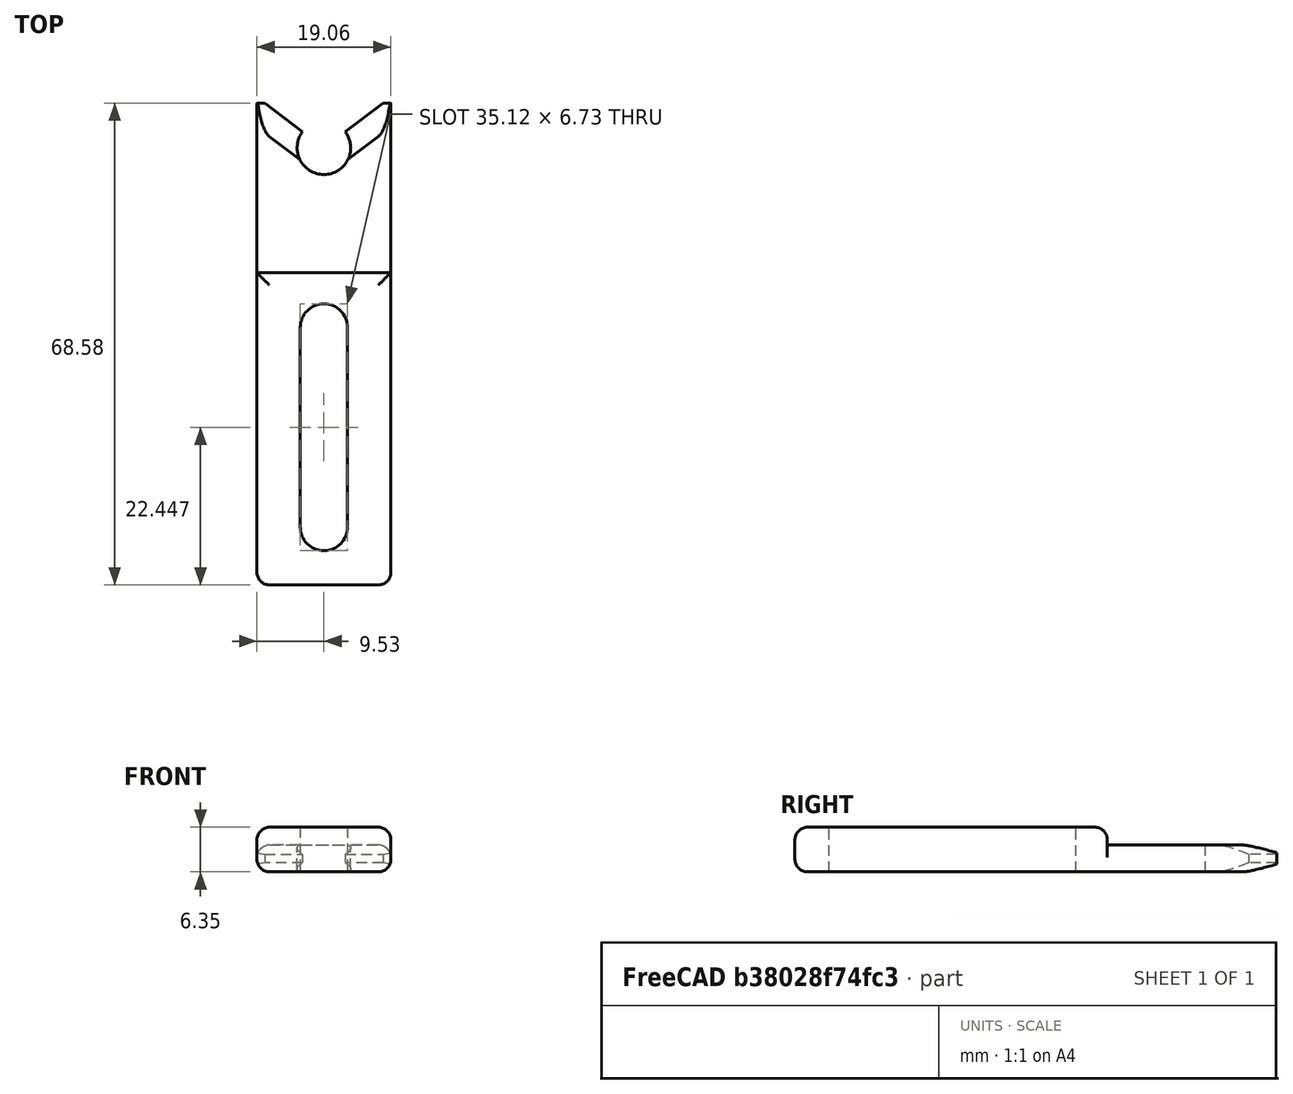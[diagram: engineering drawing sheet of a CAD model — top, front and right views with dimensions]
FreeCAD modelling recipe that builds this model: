
FCSTD DOCUMENT  (FreeCAD 0.18R16110 (Git))
Label: Headfixing clamp remodeled
License: All rights reserved
LicenseURL: http://en.wikipedia.org/wiki/All_rights_reserved
objects: Sketcher::SketchObject×6, PartDesign::SubtractivePipe×2, PartDesign::Pad×1, PartDesign::Pocket×1, Mesh::Feature×1, Part::Feature×1, PartDesign::Fillet×1, PartDesign::Body×1
note: 17 computed .brp shape members not serialized (recipe doc carries the construction recipe); baked Part::Feature solids carry a one-line shape summary decoded from their .brp

FEATURE [Sketcher::SketchObject] Sketch  label="Main body"
  MapMode = 5
  Placement = pos=(0,0,0) rot=(0.57735,0.57735,0.57735;2.0944rad)
  sketch-geometry (6):
    g0: LineSegment StartX=-62.23 StartY=6.35 StartZ=0 EndX=-17.78 EndY=6.35 EndZ=0
    g1: LineSegment StartX=-17.78 StartY=6.35 StartZ=0 EndX=-17.78 EndY=3.81 EndZ=0
    g2: LineSegment StartX=-17.78 StartY=3.81 StartZ=0 EndX=6.35 EndY=3.81 EndZ=0
    g3: LineSegment StartX=6.35 StartY=3.81 StartZ=0 EndX=6.35 EndY=0 EndZ=0
    g4: LineSegment StartX=6.35 StartY=0 StartZ=0 EndX=-62.23 EndY=0 EndZ=0
    g5: LineSegment StartX=-62.23 StartY=0 StartZ=0 EndX=-62.23 EndY=6.35 EndZ=0
  constraints (18):
    c: Coincident(g0,g1)
    c: Coincident(g1,g2)
    c: Coincident(g2,g3)
    c: Coincident(g3,g4)
    c: Coincident(g4,g5)
    c: Coincident(g0,g5)
    c: Vertical(g5)
    c: Vertical(g1)
    c: Vertical(g3)
    c: Horizontal(g0)
    c: Horizontal(g2)
    c: Horizontal(g4)
    c: DistanceY(g4) = 0
    c: Distance(g5) = 6.35
    c: DistanceX(g0) = -62.23
    c: Distance(g3) = 3.81
    c: DistanceX(g0) = -17.78
    c: DistanceX(g2) = 6.35
FEATURE [Sketcher::SketchObject] Sketch001  label="Cutouts"
  MapMode = 5
  Placement = pos=(-1e-15,0,6.35) rot=(0,0,-1;1.5708rad)
  expr: Constraints[6] = 0.265" / 2
  expr: Constraints[7] = 1.3825" - 2 * 0.1325"
  expr: Constraints[8] = 0.875" + 0.1325"
  expr: Constraints[11] = 0.331761"
  sketch-geometry (10):
    g0: ArcOfCircle CenterX=25.5905 CenterY=0 CenterZ=0 NormalX=0 NormalY=0 NormalZ=1 AngleXU=0 Radius=3.3655 StartAngle=1.5708 EndAngle=4.71239
    g1: ArcOfCircle CenterX=53.975 CenterY=0 CenterZ=0 NormalX=0 NormalY=0 NormalZ=1 AngleXU=0 Radius=3.3655 StartAngle=4.71239 EndAngle=7.85398
    g2: LineSegment StartX=25.5905 StartY=-3.3655 StartZ=0 EndX=53.975 EndY=-3.3655 EndZ=0
    g3: LineSegment StartX=25.5905 StartY=3.3655 StartZ=0 EndX=53.975 EndY=3.3655 EndZ=0
    g4: LineSegment [constr] StartX=-6.35 StartY=8.42673 StartZ=0 EndX=9e-16 EndY=0 EndZ=0
    g5: LineSegment [constr] StartX=0 StartY=0 StartZ=0 EndX=-6.35 EndY=-8.42673 EndZ=0
    g6: ArcOfCircle CenterX=0 CenterY=0 CenterZ=0 NormalX=0 NormalY=0 NormalZ=1 AngleXU=0 Radius=3.81 StartAngle=4.06662 EndAngle=8.49975
    g7: LineSegment StartX=-2.29292 StartY=-3.0428 StartZ=0 EndX=-6.35 EndY=-8.42673 EndZ=0
    g8: LineSegment StartX=-6.35 StartY=-8.42673 StartZ=0 EndX=-6.35 EndY=8.42673 EndZ=0
    g9: LineSegment StartX=-6.35 StartY=8.42673 StartZ=0 EndX=-2.29292 EndY=3.0428 EndZ=0
  constraints (25):
    c: Tangent(g0,g3) = 1.5708
    c: Tangent(g0,g2) = -1.5708
    c: Tangent(g2,g1) = -1.5708
    c: Tangent(g3,g1) = 1.5708
    c: Horizontal(g2)
    c: Equal(g0,g1)
    c: Radius(g0) = 3.3655
    c: DistanceX(g0,g1) = 28.3845
    c: DistanceX(g0) = 25.5905
    c: DistanceY(g0) = 0
    c: Symmetric(g4,g5,g-1)
    c: DistanceY(g4) = 8.42673
    c: DistanceX(g4) = -6.35
    c: Coincident(g4,g5)
    c: Coincident(g4,g6)
    c: Coincident(g4,g-1)
    c: Radius(g6) = 3.81
    c: Symmetric(g6,g6,g-1)
    c: Coincident(g7,g8)
    c: Coincident(g8,g9)
    c: Coincident(g6,g9)
    c: Coincident(g6,g7)
    c: Coincident(g5,g7)
    c: Coincident(g4,g8)
    c: Parallel(g9,g4)
FEATURE [PartDesign::Pad] Pad
  Length = 19.05
  Length2 = 99.9998
  Midplane = true
  Placement = pos=(0,0,0) rot=(0.57735,0.57735,0.57735;2.0944rad)
  Profile = -> Sketch
  Type = 0
FEATURE [PartDesign::Pocket] Pocket
  BaseFeature = -> Pad
  Length = 5.00126
  Length2 = 99.9998
  Placement = pos=(0,0,0) rot=(0.57735,0.57735,0.57735;2.0944rad)
  Profile = -> Sketch001
  Type = 1
FEATURE [Mesh::Feature] wide_post_clamp_with_slot_rescaled  label="wide post clamp with slot rescaled"
FEATURE [Part::Feature] wide_post_clamp_with_slot_rescaled001
  shape: bbox 19.05 x 68.58 x 6.35 mm, 1280 faces, 0 solids (baked)
FEATURE [Sketcher::SketchObject] Sketch002  label="Clamp V profile"
  MapMode = 5
  Placement = pos=(4e-16,6.35,-4e-16) rot=(0.57735,0.57735,0.57735;4.18879rad)
  Support = -> [Pocket]
  sketch-geometry (7):
    g0: LineSegment StartX=1.3335 StartY=-8.382 StartZ=0 EndX=2.4765 EndY=-8.382 EndZ=0
    g1: LineSegment StartX=2.4765 StartY=-8.382 StartZ=0 EndX=4.59972 EndY=-17.399 EndZ=0
    g2: LineSegment StartX=3.4925 StartY=-7.874 StartZ=0 EndX=0.3175 EndY=-7.874 EndZ=0
    g3: LineSegment StartX=-0.789722 StartY=-17.399 StartZ=0 EndX=1.3335 EndY=-8.382 EndZ=0
    g4: LineSegment [constr] StartX=1.905 StartY=0 StartZ=0 EndX=1.905 EndY=-6.35 EndZ=0
    g5: LineSegment StartX=-0.789722 StartY=-17.399 StartZ=0 EndX=0.3175 EndY=-7.874 EndZ=0
    g6: LineSegment StartX=4.59972 StartY=-17.399 StartZ=0 EndX=3.4925 EndY=-7.874 EndZ=0
  constraints (19):
    c: Coincident(g0,g1)
    c: DistanceY(g4) = -6.35
    c: DistanceX(g4) = 1.905
    c: Vertical(g4)
    c: DistanceY(g4) = 0
    c: Symmetric(g3,g1,g4)
    c: Coincident(g0,g3)
    c: Symmetric(g0,g0,g4)
    c: Angle(g3,g1) = 0.462512
    c: DistanceX(g0,g0) = 1.143
    c: DistanceY(g0,g2) = 0.508
    c: DistanceY(g0) = -8.382
    c: DistanceY(g3,g2) = 9.525
    c: Symmetric(g2,g2,g4)
    c: Coincident(g2,g6)
    c: Coincident(g1,g6)
    c: Coincident(g3,g5)
    c: Coincident(g5,g2)
    c: DistanceX(g2,g2) = 3.175
FEATURE [Sketcher::SketchObject] Sketch003  label="Clamp V path"
  MapMode = 5
  Placement = pos=(1e-16,1e-16,0) rot=(0.666877,0.332492,0.666877;3.78358rad)
  Support = -> [Pocket]
  sketch-geometry (1):
    g0: LineSegment StartX=0 StartY=-10.668 StartZ=0 EndX=0 EndY=3.175 EndZ=0
  constraints (4):
    c: DistanceX(g0) = 0
    c: DistanceY(g0) = -10.668
    c: Vertical(g0)
    c: DistanceY(g0) = 3.175
FEATURE [PartDesign::SubtractivePipe] SubtractivePipe
  AuxilleryCurvelinear = true
  AuxillerySpineTangent = false
  BaseFeature = -> Pocket
  Binormal = (0,0,0)
  Mode = 0
  Placement = pos=(0,0,0) rot=(0.57735,0.57735,0.57735;2.0944rad)
  Profile = -> Sketch002
  Spine = -> Sketch003 [Edge1]
  SpineTangent = false
  Transformation = 0
  Transition = 0
FEATURE [Sketcher::SketchObject] Sketch004  label="Clamp V profile001"
  MapMode = 5
  Placement = pos=(4e-16,6.35,-4e-16) rot=(0.57735,0.57735,0.57735;4.18879rad)
  Support = -> [Pocket]
  sketch-geometry (13):
    g0: LineSegment [constr] StartX=1.3335 StartY=-8.382 StartZ=0 EndX=2.4765 EndY=-8.382 EndZ=0
    g1: LineSegment [constr] StartX=2.4765 StartY=-8.382 StartZ=0 EndX=4.59972 EndY=-17.399 EndZ=0
    g2: LineSegment [constr] StartX=3.4925 StartY=-7.874 StartZ=0 EndX=0.3175 EndY=-7.874 EndZ=0
    g3: LineSegment [constr] StartX=-0.789722 StartY=-17.399 StartZ=0 EndX=1.3335 EndY=-8.382 EndZ=0
    g4: LineSegment [constr] StartX=1.905 StartY=0 StartZ=0 EndX=1.905 EndY=-6.35 EndZ=0
    g5: LineSegment [constr] StartX=-0.789722 StartY=-17.399 StartZ=0 EndX=0.3175 EndY=-7.874 EndZ=0
    g6: LineSegment [constr] StartX=4.59972 StartY=-17.399 StartZ=0 EndX=3.4925 EndY=-7.874 EndZ=0
    g7: LineSegment StartX=1.3335 StartY=8.382 StartZ=0 EndX=2.4765 EndY=8.382 EndZ=0
    g8: LineSegment StartX=2.4765 StartY=8.382 StartZ=0 EndX=4.59972 EndY=17.399 EndZ=0
    g9: LineSegment StartX=3.4925 StartY=7.874 StartZ=0 EndX=0.3175 EndY=7.874 EndZ=0
    g10: LineSegment StartX=-0.789722 StartY=17.399 StartZ=0 EndX=1.3335 EndY=8.382 EndZ=0
    g11: LineSegment StartX=-0.789722 StartY=17.399 StartZ=0 EndX=0.3175 EndY=7.874 EndZ=0
    g12: LineSegment StartX=4.59972 StartY=17.399 StartZ=0 EndX=3.4925 EndY=7.874 EndZ=0
  constraints (31):
    c: Coincident(g0,g1)
    c: DistanceY(g4) = -6.35
    c: DistanceX(g4) = 1.905
    c: Vertical(g4)
    c: DistanceY(g4) = 0
    c: Symmetric(g3,g1,g4)
    c: Coincident(g0,g3)
    c: Symmetric(g0,g0,g4)
    c: Angle(g3,g1) = 0.462512
    c: DistanceX(g0,g0) = 1.143
    c: DistanceY(g0,g2) = 0.508
    c: DistanceY(g0) = -8.382
    c: DistanceY(g3,g2) = 9.525
    c: Symmetric(g2,g2,g4)
    c: Coincident(g2,g6)
    c: Coincident(g1,g6)
    c: Coincident(g3,g5)
    c: Coincident(g5,g2)
    c: DistanceX(g2,g2) = 3.175
    c: Coincident(g7,g8)
    c: Coincident(g7,g10)
    c: Coincident(g9,g12)
    c: Coincident(g8,g12)
    c: Coincident(g10,g11)
    c: Coincident(g11,g9)
    c: Symmetric(g9,g2,g-1)
    c: Symmetric(g9,g2,g-1)
    c: Symmetric(g7,g0,g-1)
    c: Symmetric(g7,g0,g-1)
    c: Symmetric(g10,g3,g-1)
    c: Symmetric(g8,g1,g-1)
FEATURE [Sketcher::SketchObject] Sketch005  label="Clamp V path001"
  MapMode = 5
  Placement = pos=(3e-16,-4e-16,0) rot=(-0.407475,-0.817269,-0.407475;1.77123rad)
  Support = -> [SubtractivePipe]
  sketch-geometry (1):
    g0: LineSegment StartX=0 StartY=-10.668 StartZ=0 EndX=0 EndY=3.175 EndZ=0
  constraints (4):
    c: DistanceX(g0) = 0
    c: DistanceY(g0) = -10.668
    c: Vertical(g0)
    c: DistanceY(g0) = 3.175
FEATURE [PartDesign::SubtractivePipe] SubtractivePipe001
  AuxilleryCurvelinear = true
  AuxillerySpineTangent = false
  BaseFeature = -> SubtractivePipe
  Binormal = (0,0,0)
  Mode = 0
  Placement = pos=(0,0,0) rot=(0.57735,0.57735,0.57735;2.0944rad)
  Profile = -> Sketch004
  Spine = -> Sketch005 [Edge1]
  SpineTangent = false
  Transformation = 0
  Transition = 0
FEATURE [PartDesign::Fillet] Fillet
  Base = -> SubtractivePipe001 [Edge22,Edge16,Edge18,Edge9,Edge12,Edge11,Edge10,Edge1,Edge3,Edge2,Edge4]
  BaseFeature = -> SubtractivePipe001
  Placement = pos=(0,0,0) rot=(0.57735,0.57735,0.57735;2.0944rad)
  Radius = 1.778
FEATURE [PartDesign::Body] Body
  Group = -> [Sketch,Sketch001,Pad,Pocket,Sketch002,Sketch003,SubtractivePipe,Sketch004,Sketch005,SubtractivePipe001,Fillet]
  Origin = -> Origin
  Tip = -> Fillet
